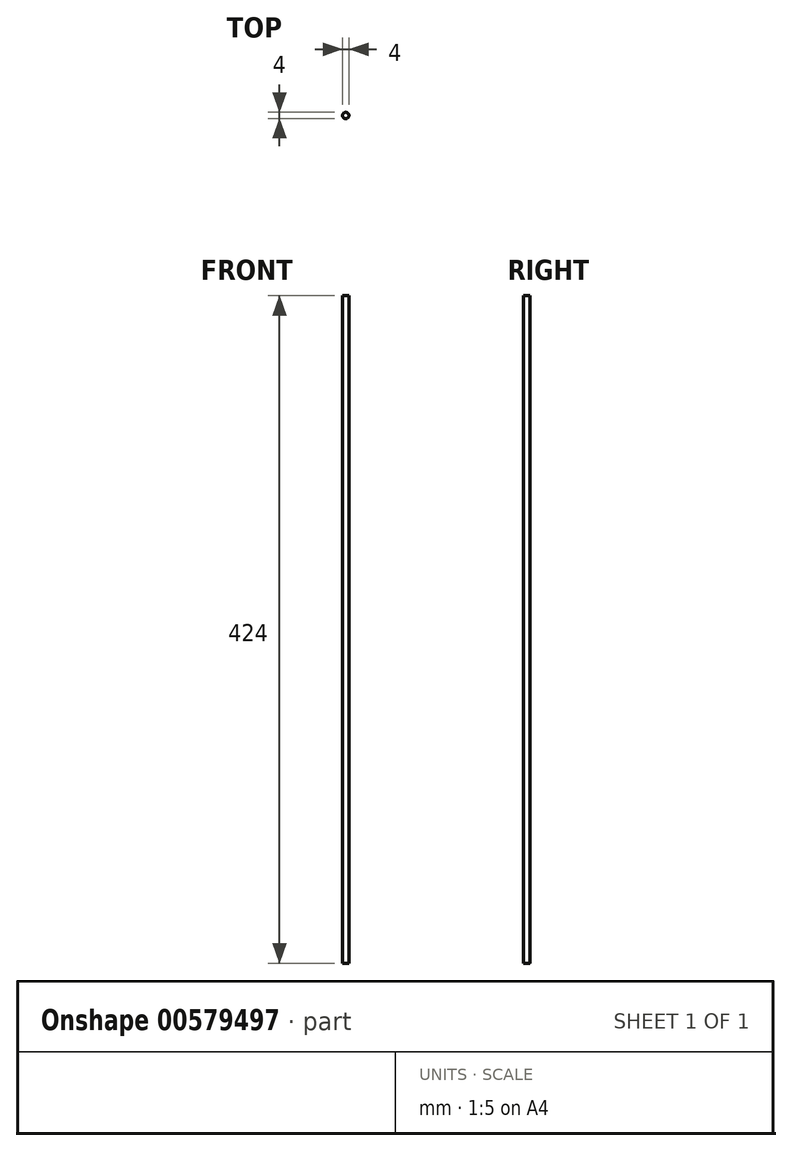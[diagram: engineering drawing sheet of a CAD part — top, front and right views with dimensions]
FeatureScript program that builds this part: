
annotation { "Feature Type Name" : "Feature", "Feature Type Description" : "" }
export const myFeature = defineFeature(function(context is Context, id is Id, definition is map)
    precondition{}
    {
        {
            var Q0;
            Q0=qCreatedBy(makeId("Top.planeOp"),FACE);
            var sketch = newSketch(context, id + "F0", { "sketchPlane" : qUnion([Q0])});
            skCircle(sketch, "E0", {"center": v(0, 0) * mm, "radius": 2 * mm});
            skSolve(sketch);
        }
        {
            var Q0;
            Q0=qSketchRegion(id+"F0",true);
            extrude(context, id + "F1", {"entities" : qUnion([Q0]), "oppositeDirection" : true, "depth" : 424 * mm, "offsetDistance" : 25 * mm});
        }
    });
